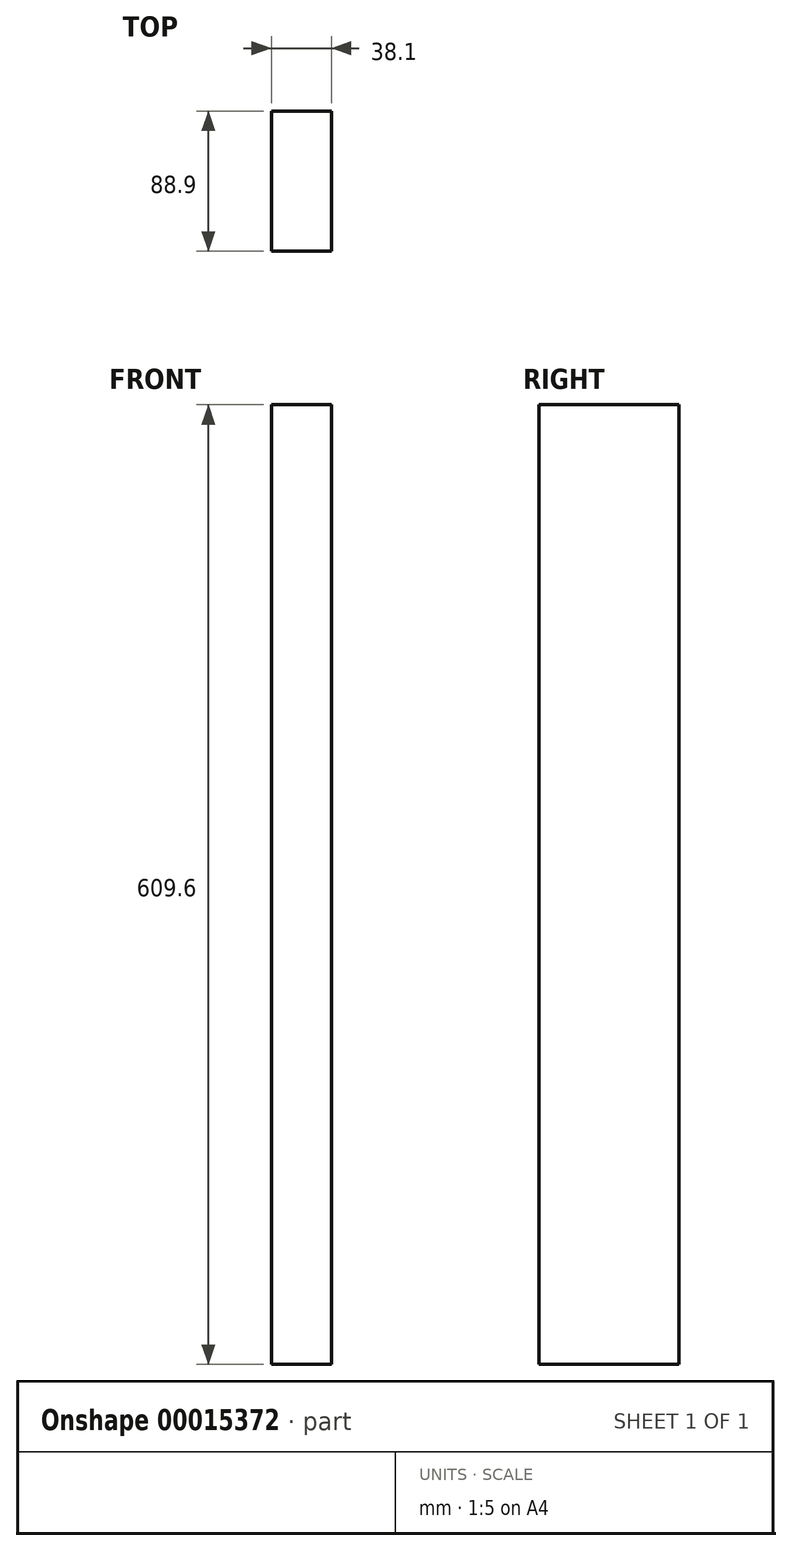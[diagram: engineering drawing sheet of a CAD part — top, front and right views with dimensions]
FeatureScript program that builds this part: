
annotation { "Feature Type Name" : "Feature", "Feature Type Description" : "" }
export const myFeature = defineFeature(function(context is Context, id is Id, definition is map)
    precondition{}
    {
        {
            var Q0;
            Q0=qCreatedBy(makeId("Top.planeOp"),FACE);
            var sketch = newSketch(context, id + "F0", { "sketchPlane" : qUnion([Q0])});
            skLineSegment(sketch, "E0.bottom", {"start": v(0, 0) * mm, "end": v(38.1, 0) * mm});
            skLineSegment(sketch, "E0.top", {"start": v(0, 88.9) * mm, "end": v(38.1, 88.9) * mm});
            skLineSegment(sketch, "E0.left", {"start": v(0, 0) * mm, "end": v(0, 88.9) * mm});
            skLineSegment(sketch, "E0.right", {"start": v(38.1, 0) * mm, "end": v(38.1, 88.9) * mm});
            skSolve(sketch);
        }
        {
            var Q0;
            Q0=makeQuery(id+"F0.imprint","IMPRINT",FACE,{"disambiguationData":[TD([[makeQuery(id+"F0.imprint","IMPRINT",EDGE,{"derivedFrom":sQuery(id+"F0.wireOp",EDGE,"E0.bottom")}),1.0]])]});
            extrude(context, id + "F1", {"entities" : qUnion([Q0]), "depth" : 609.6 * mm});
        }
    });
